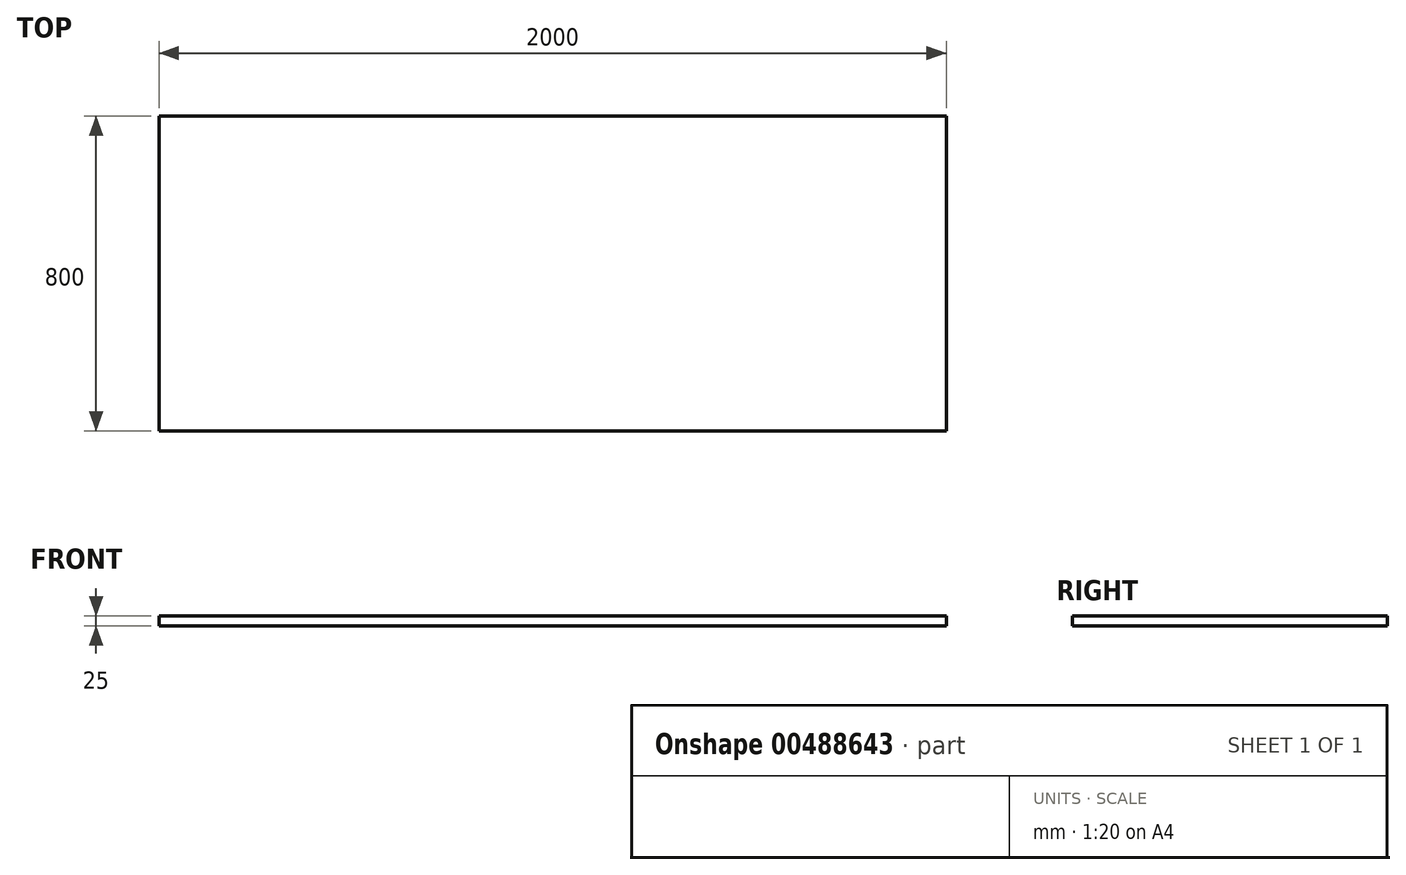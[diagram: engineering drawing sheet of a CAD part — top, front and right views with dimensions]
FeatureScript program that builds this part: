
annotation { "Feature Type Name" : "Feature", "Feature Type Description" : "" }
export const myFeature = defineFeature(function(context is Context, id is Id, definition is map)
    precondition{}
    {
        {
            var Q0;
            Q0=qCreatedBy(makeId("Top.planeOp"),FACE);
            var sketch = newSketch(context, id + "F0", { "sketchPlane" : qUnion([Q0])});
            skLineSegment(sketch, "E0.bottom", {"start": v(0, 0) * mm, "end": v(2000, 0) * mm});
            skLineSegment(sketch, "E0.top", {"start": v(0, 800) * mm, "end": v(2000, 800) * mm});
            skLineSegment(sketch, "E0.left", {"start": v(0, 0) * mm, "end": v(0, 800) * mm});
            skLineSegment(sketch, "E0.right", {"start": v(2000, 0) * mm, "end": v(2000, 800) * mm});
            skSolve(sketch);
        }
        {
            var Q0;
            Q0 = qSketchRegion(id + "F0", true);
            extrude(context, id + "F1", {"entities" : qUnion([Q0]), "depth" : 25 * mm});
        }
    });
